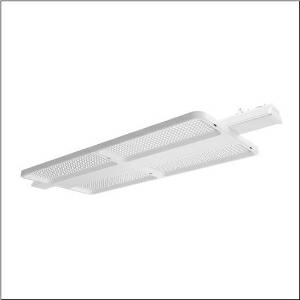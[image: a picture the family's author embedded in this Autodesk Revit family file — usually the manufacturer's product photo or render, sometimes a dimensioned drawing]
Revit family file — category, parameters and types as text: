
# Revit family: highbay_21_fur_licross_r__tragschiene_maxi_52hn11db3pla_6a31
name_source: partatom
category: Lighting Fixtures
units: mm (PartAtom-declared; Revit-internal decimal feet)

## family parameters
Cut with Voids When Loaded = No
Host = Face
Light Source = No
Part Type = Normal
Room Calculation Point = No
Round Connector Dimension = Use Diameter
Shared = No

## types (1)
- --- (1 x LED, 5350 lm, 31.4 W, 3000K)
    Apparent Load = 31 VA
    CIE Flux Codes = 89 97 99 100 100
    Color Rendering = 80
    Color Temperature = 3000K
    Default Elevation = 1800 mm
    Description = high bay luminaire Highbay 21 for Licross® trunking rail maxi; direct symmetric narrow distribution, light control with lens of PMMA; UGR ≤ 22 (X = 4H | Y = 8H | S = 0.25H | reflection values 70/50/20); luminous flux: 34.690lm; light colour: 830, colour temperature: 3000K, MacAdam ≤ 3 SDCM (initial), colour rendering: CRI > 80; luminous efficacy: 175,5lm/W; rated service life: 75.000h (L80/B50) at AT= ta max; control: DALI 2; luminaire connection: plug, 5-pole, with phase selectionmains connection: 230..240V, AC 50/60Hz; connected load: 197,7W; protection rating (complete): IP64; insulation class (complete): insulation class I (protective earthing); protection symbol: D; impact resistance: IK07; certification: CE, ENEC, VDE, UKCA; internal wiring halogen-free; luminaire corresponds to IFS (International Featured Standards) requirements for safety and quality in the food industry; LABS conformity tested according to VDMA 24364:2018-05; housing frame of high-performance plastic PA6, matt traffic white (RAL 9016); cover of PMMA; fixing on rail side of steel, galvanised, white; blank cover of PC/ABS, traffic white (RAL 9016); dimension (LxWxH): 1.250 x 442 x 71mm; permissible operating ambient temperature: -40..+55°C (reducing of maximum allowable ambient temperature of 5°C with ceiling mounting); packaging unit: 1 piece
    Height = 72 mm  [stored 0.23622 ft]
    Lamp = 1 x LED
    Lamp Light Flux = 5350 lm
    Lamp Power = 31.4 W
    Lamp count = 1
    Length = 946 mm
    Luminous efficacy = 170 lm/W
    Manufacturer = Siteco
    ModVariant = No
    Model = 52HN11DB3PLA
    Mounting Place = Ceiling
    Mounting Type = Pendant
    Number of Poles = 1
    OnlyDefault = Yes
    Power Factor = 1
    Product Name = Highbay 21 für Licross® Tragschiene maxi
    Product group = high bay luminaire
    ProductGroupID = 901
    Protection Class = Protection class I
    Protection Degree = IP 64
    RLX_Detail_Level = 1
    RLX_Emergency_Light_Flux = 0 lm
    RLX_Emergency_Type = 0
    RLX_Emergency_Type_DB = No
    RlxData = <blob elided: 130577 chars, md5=8e72a815>
    Socket = socket
    Standby Power = 0 W
    System Light Flux = 5350 lm
    System Power = 31 W
    Type Comments = : DC mode (central or group accumulator) initial emergency light level
    Type Image = l_1361711.jpg
    URL = http://relux.com
    VarID = @adj_000993
    Voltage = 0 V
    Weight = 0.00 kg
    Width = 442 mm

note: [stored X ft] marks values corroborated as IEEE doubles in the binary element streams (Revit-internal decimal feet)

## geometry (parser evidence)
native form markers: Blend x4, Sweep x10
no freeform markers — native parametric forms only
